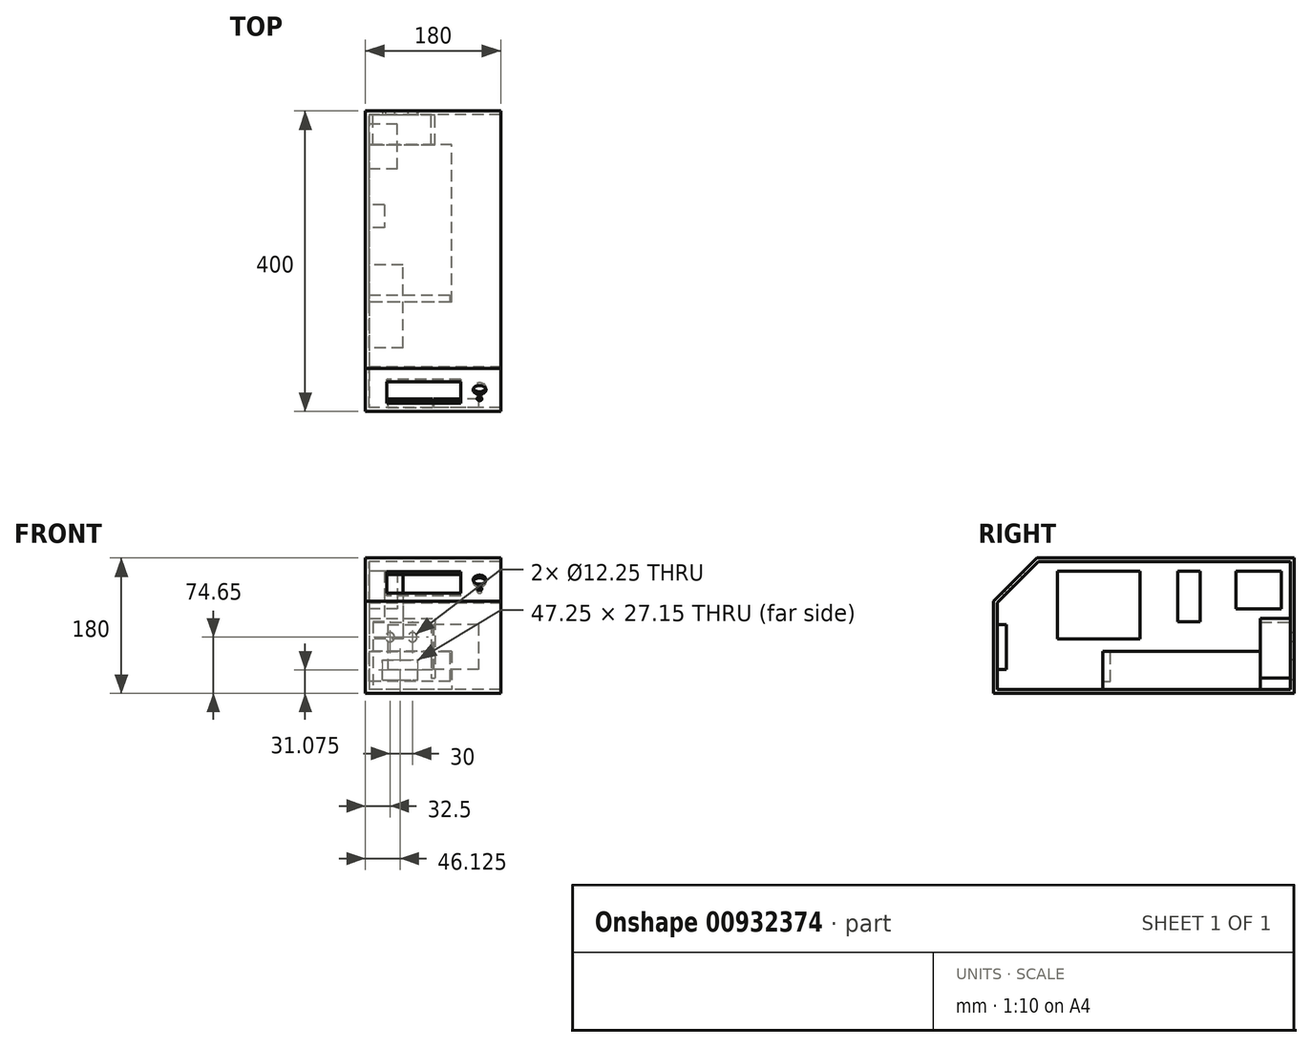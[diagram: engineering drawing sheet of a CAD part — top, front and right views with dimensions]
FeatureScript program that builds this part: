
annotation { "Feature Type Name" : "Feature", "Feature Type Description" : "" }
export const myFeature = defineFeature(function(context is Context, id is Id, definition is map)
    precondition{}
    {
        {
            var Q0;
            Q0=qCreatedBy(makeId("Front.planeOp"),FACE);
            var sketch = newSketch(context, id + "F0", { "sketchPlane" : qUnion([Q0])});
            skLineSegment(sketch, "E0.bottom", {"start": v(90, 90) * mm, "end": v(-90, 90) * mm});
            skLineSegment(sketch, "E0.top", {"start": v(90, -90) * mm, "end": v(-90, -90) * mm});
            skLineSegment(sketch, "E0.left", {"start": v(90, 90) * mm, "end": v(90, -90) * mm});
            skLineSegment(sketch, "E0.right", {"start": v(-90, 90) * mm, "end": v(-90, -90) * mm});
            skPoint(sketch, "E0.middle", {"position": v(0, 0) * mm});
            skSolve(sketch);
        }
        {
            var Q0;
            Q0=makeQuery(id+"F0.imprint","IMPRINT",FACE,{"disambiguationData":[TD([[makeQuery(id+"F0.imprint","IMPRINT",EDGE,{"derivedFrom":sQuery(id+"F0.wireOp",EDGE,"E0.bottom")}),1.0]])]});
            extrude(context, id + "F1", {"entities" : qUnion([Q0]), "oppositeDirection" : true, "depth" : 400 * mm, "offsetDistance" : 25.4 * mm});
        }
        {
            var Q0;
            Q0=qCreatedBy(makeId("Right.planeOp"),FACE);
            var sketch = newSketch(context, id + "F2", { "sketchPlane" : qUnion([Q0])});
            skLineSegment(sketch, "E1", {"start": v(0, 90) * mm, "end": v(57.63, 90) * mm});
            skLineSegment(sketch, "E2", {"start": v(57.63, 90) * mm, "end": v(0, 32.37) * mm});
            skLineSegment(sketch, "E3", {"start": v(0, 32.37) * mm, "end": v(0, 90) * mm});
            skSolve(sketch);
        }
        {
            var Q0;
            Q0 = qSketchRegion(id + "F2", true);
            extrude(context, id + "F3", {"entities" : qUnion([Q0]), "operationType" : NewBodyOperationType.REMOVE, "endBound" : BoundingType.THROUGH_ALL, "oppositeDirection" : true, "depth" : 25.4 * mm, "offsetDistance" : 25.4 * mm, "hasSecondDirection" : true, "secondDirectionBound" : BoundingType.THROUGH_ALL, "secondDirectionOppositeDirection" : false, "secondDirectionDepth" : 25.4 * mm});
        }
        {
            var Q0;
            Q0=makeQuery(id+"F1.opExtrude","SWEPT_FACE",FACE,{"disambiguationData":[OSD([sQuery(id+"F0.wireOp",EDGE,"E0.left")])]});
            var Q1;
            Q1=makeQuery(id+"F1.opExtrude","SWEPT_BODY",BODY,{"disambiguationData":[OSD([sQuery(id+"F0.wireOp",EDGE,"E0.bottom"),sQuery(id+"F0.wireOp",EDGE,"E0.top"),sQuery(id+"F0.wireOp",EDGE,"E0.left"),sQuery(id+"F0.wireOp",EDGE,"E0.right")])]});
            shell(context, id + "F4", {"entities" : qUnion([Q0]), "parts" : qUnion([Q1]), "thickness" : 5 * mm});
        }
        {
            var Q0;
            Q0=makeQuery(id+"F3.boolean.opBoolean","COPY",FACE,{"derivedFrom":makeQuery(id+"F3.opExtrude","SWEPT_FACE",FACE,{"disambiguationData":[OSD([sQuery(id+"F2.wireOp",EDGE,"E2")])]})});
            var sketch = newSketch(context, id + "F5", { "sketchPlane" : qUnion([Q0])});
            skLineSegment(sketch, "E4.bottom", {"start": v(-61.75, 78.64) * mm, "end": v(36.75, 78.64) * mm});
            skLineSegment(sketch, "E4.top", {"start": v(-61.75, 38.14) * mm, "end": v(36.75, 38.14) * mm});
            skLineSegment(sketch, "E4.left", {"start": v(-61.75, 78.64) * mm, "end": v(-61.75, 38.14) * mm});
            skLineSegment(sketch, "E4.right", {"start": v(36.75, 78.64) * mm, "end": v(36.75, 38.14) * mm});
            skCircle(sketch, "E5", {"center": v(61.75, 63.64) * mm, "radius": 8.5 * mm});
            skCircle(sketch, "E6", {"center": v(61.75, 46.64) * mm, "radius": 3.25 * mm});
            skSolve(sketch);
        }
        {
            var Q0;
            Q0 = qSketchRegion(id + "F5", true);
            extrude(context, id + "F6", {"entities" : qUnion([Q0]), "operationType" : NewBodyOperationType.REMOVE, "endBound" : BoundingType.UP_TO_NEXT, "oppositeDirection" : true, "depth" : 25 * mm, "offsetDistance" : 25 * mm});
        }
        {
            var Q0;
            {var subQ0=sQuery(id+"F0.wireOp",EDGE,"E0.right");var subQ1=sQuery(id+"F0.wireOp",EDGE,"E0.left");var subQ2=sQuery(id+"F0.wireOp",EDGE,"E0.top");var subQ3=sQuery(id+"F0.wireOp",EDGE,"E0.bottom");Q0=makeQuery(id+"F4.opShell","OFFSET_FACE",FACE,{"disambiguationData":[OSD([subQ3,subQ2,subQ1,subQ0]),TDD([makeQuery(id+"F1.opExtrude","CAP_FACE",FACE,{"disambiguationData":[OSD([subQ3,subQ2,subQ1,subQ0])],"isStart":true})])]});}
            var sketch = newSketch(context, id + "F7", { "sketchPlane" : qUnion([Q0])});
            skLineSegment(sketch, "E7.bottom", {"start": v(-60.5, 1.53) * mm, "end": v(-0.5, 1.53) * mm});
            skLineSegment(sketch, "E7.top", {"start": v(-60.5, -58.47) * mm, "end": v(-0.5, -58.47) * mm});
            skLineSegment(sketch, "E7.left", {"start": v(-60.5, 1.53) * mm, "end": v(-60.5, -58.47) * mm});
            skLineSegment(sketch, "E7.right", {"start": v(-0.5, 1.53) * mm, "end": v(-0.5, -58.47) * mm});
            skLineSegment(sketch, "E8", {"start": v(-60.5, -28.47) * mm, "end": v(-84.75, -28.47) * mm, "construction": true});
            skPoint(sketch, "E8.endSnap0", {"position": v(-84.75, -28.47) * mm});
            skLineSegment(sketch, "E9.MirrorCS", {"start": v(60.5, -28.47) * mm, "end": v(84.75, -28.47) * mm, "construction": true});
            skPoint(sketch, "E10.MirrorP", {"position": v(84.75, -28.47) * mm});
            skLineSegment(sketch, "E11.MirrorCS", {"start": v(60.5, 1.53) * mm, "end": v(0.5, 1.53) * mm});
            skLineSegment(sketch, "E12.MirrorCS", {"start": v(0.5, 1.53) * mm, "end": v(0.5, -58.47) * mm});
            skLineSegment(sketch, "E13.MirrorCS", {"start": v(60.5, -58.47) * mm, "end": v(0.5, -58.47) * mm});
            skLineSegment(sketch, "E14.MirrorCS", {"start": v(60.5, 1.53) * mm, "end": v(60.5, -58.47) * mm});
            skSolve(sketch);
        }
        {
            var Q0;
            Q0 = qSketchRegion(id + "F7", true);
            extrude(context, id + "F8", {"entities" : qUnion([Q0]), "depth" : 12 * mm, "offsetDistance" : 25 * mm});
        }
        {
            var Q0;
            {var subQ0=sQuery(id+"F0.wireOp",EDGE,"E0.right");var subQ1=sQuery(id+"F0.wireOp",EDGE,"E0.left");var subQ2=sQuery(id+"F0.wireOp",EDGE,"E0.top");var subQ3=sQuery(id+"F0.wireOp",EDGE,"E0.bottom");Q0=makeQuery(id+"F4.opShell","OFFSET_FACE",FACE,{"disambiguationData":[OSD([subQ3,subQ2,subQ1,subQ0]),TDD([makeQuery(id+"F1.opExtrude","CAP_FACE",FACE,{"disambiguationData":[OSD([subQ3,subQ2,subQ1,subQ0])],"isStart":false})])]});}
            var sketch = newSketch(context, id + "F9", { "sketchPlane" : qUnion([Q0])});
            skLineSegment(sketch, "E15.bottom", {"start": v(-67.5, -72.5) * mm, "end": v(-20.25, -72.5) * mm});
            skLineSegment(sketch, "E15.top", {"start": v(-67.5, -45.35) * mm, "end": v(-20.25, -45.35) * mm});
            skLineSegment(sketch, "E15.left", {"start": v(-67.5, -72.5) * mm, "end": v(-67.5, -45.35) * mm});
            skLineSegment(sketch, "E15.right", {"start": v(-20.25, -72.5) * mm, "end": v(-20.25, -45.35) * mm});
            skCircle(sketch, "E16", {"center": v(-57.5, -15.35) * mm, "radius": 6.12 * mm});
            skCircle(sketch, "E17", {"center": v(-27.5, -15.35) * mm, "radius": 6.12 * mm});
            skSolve(sketch);
        }
        {
            var Q0;
            Q0 = qSketchRegion(id + "F9", true);
            extrude(context, id + "F10", {"entities" : qUnion([Q0]), "operationType" : NewBodyOperationType.REMOVE, "endBound" : BoundingType.THROUGH_ALL, "oppositeDirection" : true, "depth" : 25 * mm, "offsetDistance" : 25 * mm});
        }
        {
            var Q0;
            {var subQ0=sQuery(id+"F0.wireOp",EDGE,"E0.right");var subQ1=sQuery(id+"F0.wireOp",EDGE,"E0.left");var subQ2=sQuery(id+"F0.wireOp",EDGE,"E0.top");var subQ3=sQuery(id+"F0.wireOp",EDGE,"E0.bottom");Q0=makeQuery(id+"F4.opShell","OFFSET_FACE",FACE,{"disambiguationData":[OSD([subQ3,subQ2,subQ1,subQ0]),TDD([makeQuery(id+"F1.opExtrude","CAP_FACE",FACE,{"disambiguationData":[OSD([subQ3,subQ2,subQ1,subQ0])],"isStart":false})])]});}
            var sketch = newSketch(context, id + "F11", { "sketchPlane" : qUnion([Q0])});
            skLineSegment(sketch, "E18.bottom", {"start": v(-80, 4.65) * mm, "end": v(-2.75, 4.65) * mm});
            skLineSegment(sketch, "E18.top", {"start": v(-85, 9.65) * mm, "end": v(2.25, 9.65) * mm});
            skLineSegment(sketch, "E19.left", {"start": v(-2.75, 4.65) * mm, "end": v(-2.75, -70) * mm});
            skLineSegment(sketch, "E19.right", {"start": v(2.25, 9.65) * mm, "end": v(2.25, -70) * mm});
            skLineSegment(sketch, "E20", {"start": v(-2.75, -70) * mm, "end": v(2.25, -70) * mm});
            skLineSegment(sketch, "E21.top", {"start": v(-85, -85) * mm, "end": v(-80, -85) * mm});
            skLineSegment(sketch, "E21.left", {"start": v(-85, 9.65) * mm, "end": v(-85, -85) * mm});
            skLineSegment(sketch, "E21.right", {"start": v(-80, 4.65) * mm, "end": v(-80, -85) * mm});
            skSolve(sketch);
        }
        {
            var Q0;
            Q0 = qSketchRegion(id + "F11", true);
            extrude(context, id + "F12", {"entities" : qUnion([Q0]), "operationType" : NewBodyOperationType.ADD, "depth" : 40 * mm, "offsetDistance" : 25 * mm});
        }
        {
            var Q0;
            Q0=makeQuery(id+"F12.opExtrude","CAP_FACE",FACE,{"disambiguationData":[OSD([sQuery(id+"F11.wireOp",EDGE,"E18.bottom"),sQuery(id+"F11.wireOp",EDGE,"E18.top"),sQuery(id+"F11.wireOp",EDGE,"E18.left"),sQuery(id+"F11.wireOp",EDGE,"E19.left"),sQuery(id+"F11.wireOp",EDGE,"E19.right"),sQuery(id+"F11.wireOp",EDGE,"E20")])],"isStart":false});
            var sketch = newSketch(context, id + "F13", { "sketchPlane" : qUnion([Q0])});
            skLineSegment(sketch, "E22.bottom", {"start": v(24.86, -34.2) * mm, "end": v(-85, -34.2) * mm});
            skLineSegment(sketch, "E22.top", {"start": v(24.86, -85) * mm, "end": v(-85, -85) * mm});
            skLineSegment(sketch, "E22.left", {"start": v(24.86, -34.2) * mm, "end": v(24.86, -85) * mm});
            skLineSegment(sketch, "E22.right", {"start": v(-85, -34.2) * mm, "end": v(-85, -85) * mm});
            skPoint(sketch, "E22.middle", {"position": v(-30.07, -59.6) * mm});
            skSolve(sketch);
        }
        {
            var Q0;
            Q0 = qSketchRegion(id + "F13", true);
            extrude(context, id + "F14", {"entities" : qUnion([Q0]), "depth" : 209.55 * mm, "offsetDistance" : 25 * mm});
        }
        {
            var Q0;
            Q0=makeQuery(id+"F14.opExtrude","SWEPT_FACE",FACE,{"disambiguationData":[OSD([sQuery(id+"F13.wireOp",EDGE,"E22.bottom")])]});
            var sketch = newSketch(context, id + "F15", { "sketchPlane" : qUnion([Q0])});
            skLineSegment(sketch, "E23.bottom", {"start": v(-85, 145.45) * mm, "end": v(22.86, 145.45) * mm});
            skLineSegment(sketch, "E23.top", {"start": v(-85, 155.45) * mm, "end": v(22.86, 155.45) * mm});
            skLineSegment(sketch, "E23.left", {"start": v(-85, 145.45) * mm, "end": v(-85, 155.45) * mm});
            skLineSegment(sketch, "E23.right", {"start": v(22.86, 145.45) * mm, "end": v(22.86, 155.45) * mm});
            skSolve(sketch);
        }
        {
            var Q0;
            Q0 = qSketchRegion(id + "F15", true);
            extrude(context, id + "F16", {"entities" : qUnion([Q0]), "operationType" : NewBodyOperationType.REMOVE, "oppositeDirection" : true, "depth" : 40 * mm, "offsetDistance" : 25 * mm});
        }
        {
            var Q0;
            Q0=makeQuery(id+"F4.opShell","OFFSET_FACE",FACE,{"disambiguationData":[OSD([sQuery(id+"F0.wireOp",EDGE,"E0.right")])]});
            var sketch = newSketch(context, id + "F17", { "sketchPlane" : qUnion([Q0])});
            skLineSegment(sketch, "E24.bottom", {"start": v(322.5, 72.5) * mm, "end": v(382.5, 72.5) * mm});
            skLineSegment(sketch, "E24.top", {"start": v(322.5, 22.5) * mm, "end": v(382.5, 22.5) * mm});
            skLineSegment(sketch, "E24.left", {"start": v(322.5, 72.5) * mm, "end": v(322.5, 22.5) * mm});
            skLineSegment(sketch, "E24.right", {"start": v(382.5, 72.5) * mm, "end": v(382.5, 22.5) * mm});
            skSolve(sketch);
        }
        {
            var Q0;
            Q0 = qSketchRegion(id + "F17", true);
            extrude(context, id + "F18", {"entities" : qUnion([Q0]), "depth" : 37.5 * mm, "offsetDistance" : 25 * mm});
        }
        {
            var Q0;
            Q0=makeQuery(id+"F4.opShell","OFFSET_FACE",FACE,{"disambiguationData":[OSD([sQuery(id+"F0.wireOp",EDGE,"E0.right")])]});
            var sketch = newSketch(context, id + "F19", { "sketchPlane" : qUnion([Q0])});
            skLineSegment(sketch, "E25.bottom", {"start": v(275, 72.5) * mm, "end": v(245, 72.5) * mm});
            skLineSegment(sketch, "E25.top", {"start": v(275, 5) * mm, "end": v(245, 5) * mm});
            skLineSegment(sketch, "E25.left", {"start": v(275, 72.5) * mm, "end": v(275, 5) * mm});
            skLineSegment(sketch, "E25.right", {"start": v(245, 72.5) * mm, "end": v(245, 5) * mm});
            skSolve(sketch);
        }
        {
            var Q0;
            Q0=makeQuery(id+"F19.imprint","IMPRINT",FACE,{"disambiguationData":[TD([[makeQuery(id+"F19.imprint","IMPRINT",EDGE,{"derivedFrom":sQuery(id+"F19.wireOp",EDGE,"E25.bottom")}),1.0]])]});
            extrude(context, id + "F20", {"entities" : qUnion([Q0]), "depth" : 20 * mm, "offsetDistance" : 25 * mm});
        }
        {
            var Q0;
            Q0=makeQuery(id+"F4.opShell","OFFSET_FACE",FACE,{"disambiguationData":[OSD([sQuery(id+"F0.wireOp",EDGE,"E0.right")])]});
            var sketch = newSketch(context, id + "F21", { "sketchPlane" : qUnion([Q0])});
            skLineSegment(sketch, "E26.bottom", {"start": v(85, 72.5) * mm, "end": v(195, 72.5) * mm});
            skLineSegment(sketch, "E26.top", {"start": v(85, -17.5) * mm, "end": v(195, -17.5) * mm});
            skLineSegment(sketch, "E26.left", {"start": v(85, 72.5) * mm, "end": v(85, -17.5) * mm});
            skLineSegment(sketch, "E26.right", {"start": v(195, 72.5) * mm, "end": v(195, -17.5) * mm});
            skSolve(sketch);
        }
        {
            var Q0;
            Q0=makeQuery(id+"F21.imprint","IMPRINT",FACE,{"disambiguationData":[TD([[makeQuery(id+"F21.imprint","IMPRINT",EDGE,{"derivedFrom":sQuery(id+"F21.wireOp",EDGE,"E26.bottom")}),-1.0]])]});
            extrude(context, id + "F22", {"entities" : qUnion([Q0]), "depth" : 45 * mm, "offsetDistance" : 25 * mm});
        }
    });
